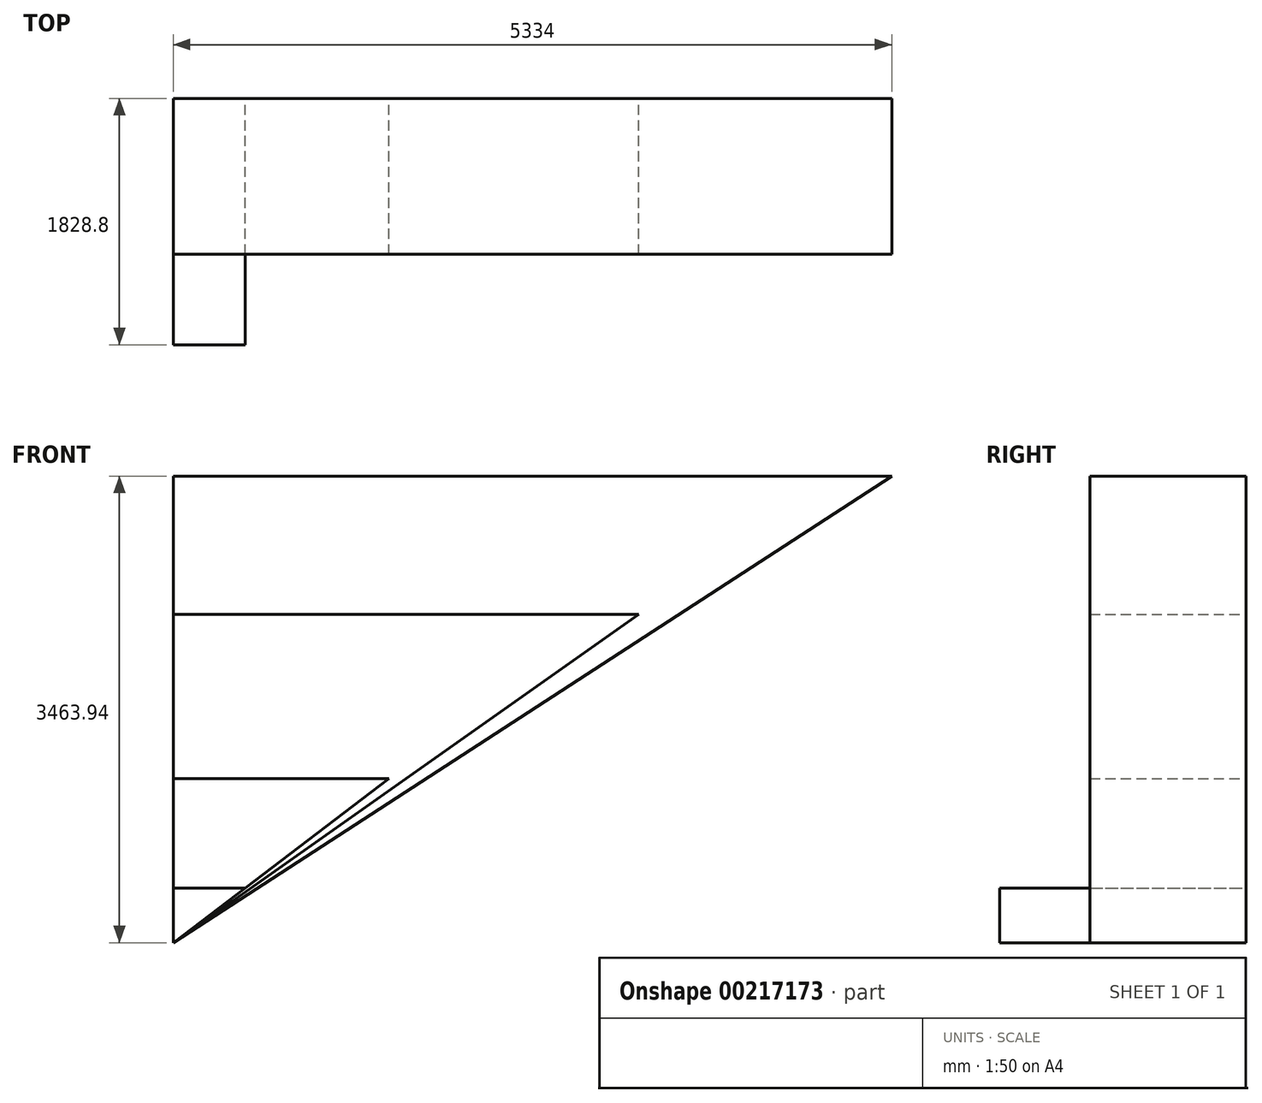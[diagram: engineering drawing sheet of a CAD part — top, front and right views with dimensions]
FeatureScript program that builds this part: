
annotation { "Feature Type Name" : "Feature", "Feature Type Description" : "" }
export const myFeature = defineFeature(function(context is Context, id is Id, definition is map)
    precondition{}
    {
        {
            var Q0;
            Q0=qCreatedBy(makeId("Front.planeOp"),FACE);
            var sketch = newSketch(context, id + "F0", { "sketchPlane" : qUnion([Q0])});
            skLineSegment(sketch, "E0", {"start": v(0, 0) * mm, "end": v(0, 3463.94) * mm});
            skLineSegment(sketch, "E1", {"start": v(0, 3463.94) * mm, "end": v(5334, 3463.94) * mm});
            skLineSegment(sketch, "E2", {"start": v(5334, 3463.94) * mm, "end": v(0, 0) * mm});
            skSolve(sketch);
        }
        {
            var Q0;
            Q0 = qSketchRegion(id + "F0", true);
            extrude(context, id + "F1", {"entities" : qUnion([Q0]), "depth" : 1158.24 * mm});
        }
        {
            var Q0;
            Q0=qCreatedBy(makeId("Front.planeOp"),FACE);
            var sketch = newSketch(context, id + "F2", { "sketchPlane" : qUnion([Q0])});
            skLineSegment(sketch, "E3", {"start": v(0, 0) * mm, "end": v(0, 2438.4) * mm});
            skLineSegment(sketch, "E4", {"start": v(0, 2438.4) * mm, "end": v(3454.4, 2438.4) * mm});
            skLineSegment(sketch, "E5", {"start": v(3454.4, 2438.4) * mm, "end": v(0, 0) * mm});
            skSolve(sketch);
        }
        {
            var Q0;
            Q0 = qSketchRegion(id + "F2", true);
            extrude(context, id + "F3", {"entities" : qUnion([Q0]), "depth" : 1158.24 * mm});
        }
        {
            var Q0;
            Q0=qCreatedBy(makeId("Front.planeOp"),FACE);
            var sketch = newSketch(context, id + "F4", { "sketchPlane" : qUnion([Q0])});
            skLineSegment(sketch, "E6", {"start": v(0, 0) * mm, "end": v(0, 1219.2) * mm});
            skLineSegment(sketch, "E7", {"start": v(0, 1219.2) * mm, "end": v(1600.2, 1219.2) * mm});
            skLineSegment(sketch, "E8", {"start": v(1600.2, 1219.2) * mm, "end": v(0, 0) * mm});
            skSolve(sketch);
        }
        {
            var Q0;
            Q0 = qSketchRegion(id + "F4", true);
            extrude(context, id + "F5", {"entities" : qUnion([Q0]), "depth" : 1158.24 * mm});
        }
        {
            var Q0;
            Q0=qCreatedBy(makeId("Front.planeOp"),FACE);
            var sketch = newSketch(context, id + "F6", { "sketchPlane" : qUnion([Q0])});
            skLineSegment(sketch, "E9", {"start": v(0, 0) * mm, "end": v(0, 406.4) * mm});
            skLineSegment(sketch, "E10", {"start": v(0, 406.4) * mm, "end": v(533.4, 406.4) * mm});
            skLineSegment(sketch, "E11", {"start": v(533.4, 406.4) * mm, "end": v(0, 0) * mm});
            skSolve(sketch);
        }
        {
            var Q0;
            Q0 = qSketchRegion(id + "F6", true);
            extrude(context, id + "F7", {"entities" : qUnion([Q0]), "depth" : 1828.8 * mm});
        }
    });
